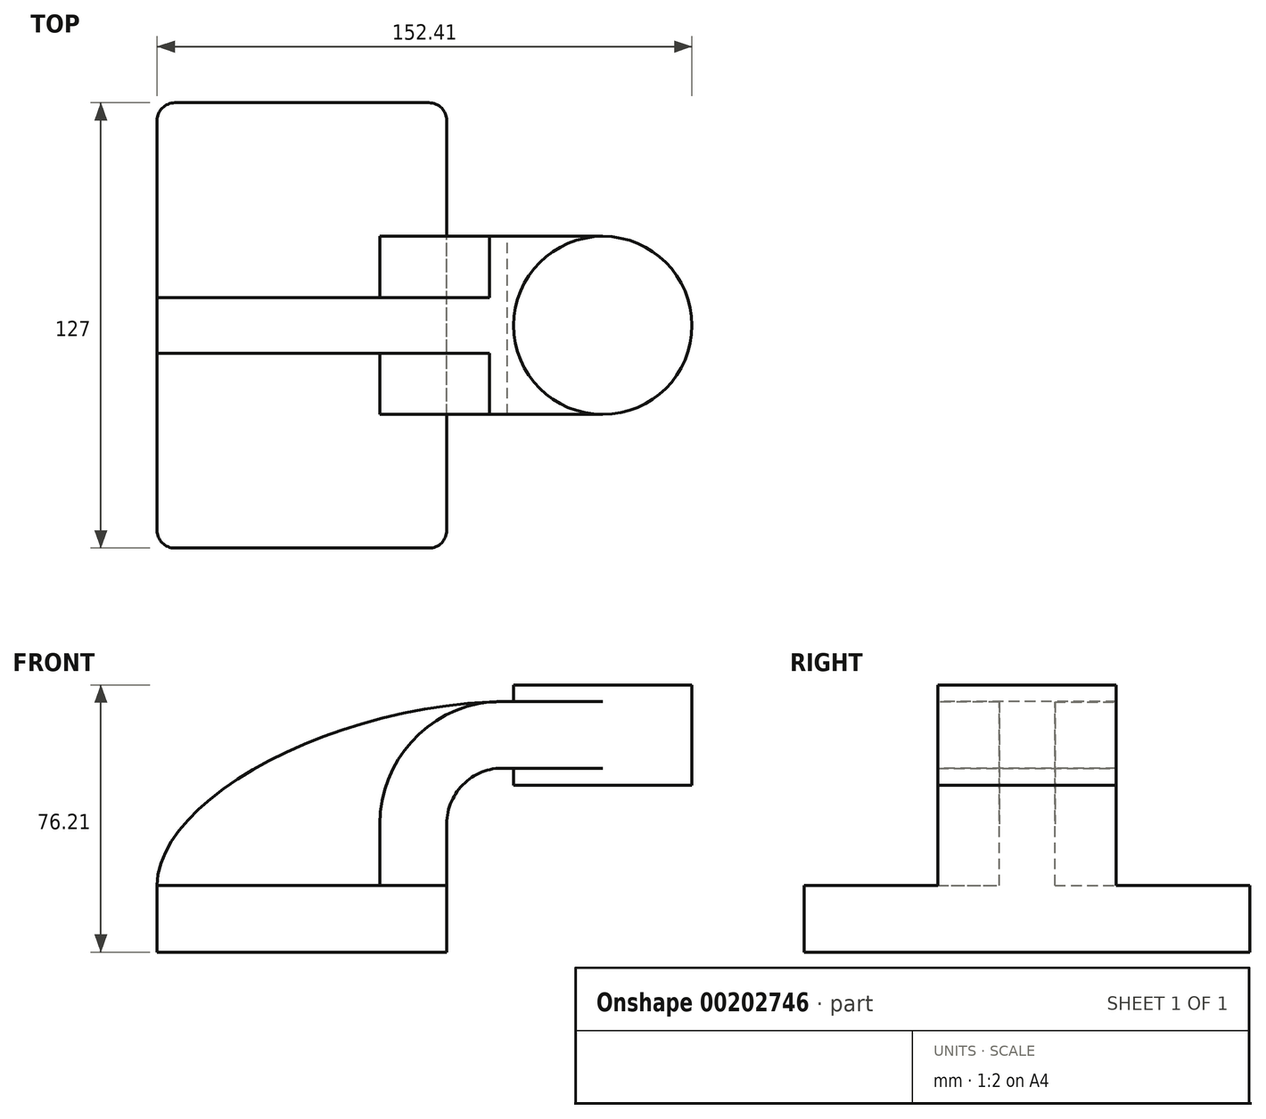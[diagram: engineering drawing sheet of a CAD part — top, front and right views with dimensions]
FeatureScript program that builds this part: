
annotation { "Feature Type Name" : "Feature", "Feature Type Description" : "" }
export const myFeature = defineFeature(function(context is Context, id is Id, definition is map)
    precondition{}
    {
        {
            var Q0;
            Q0=qCreatedBy(makeId("Front.planeOp"),FACE);
            var sketch = newSketch(context, id + "F0", { "sketchPlane" : qUnion([Q0])});
            skLineSegment(sketch, "E0.bottom", {"start": v(-41.28, 9.52) * mm, "end": v(41.28, 9.53) * mm});
            skLineSegment(sketch, "E0.top", {"start": v(-41.28, -9.53) * mm, "end": v(41.28, -9.53) * mm});
            skLineSegment(sketch, "E0.left", {"start": v(-41.28, 9.52) * mm, "end": v(-41.28, -9.53) * mm});
            skLineSegment(sketch, "E0.right", {"start": v(41.28, 9.53) * mm, "end": v(41.28, -9.52) * mm});
            skPoint(sketch, "E0.middle", {"position": v(0, 0) * mm});
            skLineSegment(sketch, "E1.bottom", {"start": v(111.12, 38.1) * mm, "end": v(60.32, 38.1) * mm});
            skLineSegment(sketch, "E1.top", {"start": v(111.12, 66.67) * mm, "end": v(60.32, 66.67) * mm});
            skLineSegment(sketch, "E1.left", {"start": v(111.12, 38.1) * mm, "end": v(111.12, 66.68) * mm});
            skLineSegment(sketch, "E1.right", {"start": v(60.32, 38.1) * mm, "end": v(60.32, 66.67) * mm});
            skPoint(sketch, "E1.middle", {"position": v(85.72, 52.39) * mm});
            skLineSegment(sketch, "E2", {"start": v(41.27, 9.53) * mm, "end": v(41.27, 27.06) * mm});
            skArc(sketch, "E3", {"start": v(41.27, 27.06) * mm, "mid": v(46.4, 38.74) * mm, "end": v(58.47, 42.88) * mm});
            skLineSegment(sketch, "E4", {"start": v(58.47, 42.88) * mm, "end": v(83.46, 42.88) * mm});
            skLineSegment(sketch, "E5.0", {"start": v(59.11, 61.93) * mm, "end": v(83.46, 61.93) * mm});
            skArc(sketch, "E5.1", {"start": v(22.22, 27.06) * mm, "mid": v(33.16, 52.44) * mm, "end": v(59.11, 61.93) * mm});
            skLineSegment(sketch, "E5.2", {"start": v(22.22, 9.53) * mm, "end": v(22.22, 27.06) * mm});
            skFitSpline(sketch, "E6", {"points": [v(-41.28, 9.52) * mm, v(59.11, 61.93) * mm], "startDerivative": vector(0.16, 74.33) * mm, "endDerivative": vector(148.19, 0.72) * mm});
            skLineSegment(sketch, "E7", {"start": v(85.72, 66.67) * mm, "end": v(85.72, 38.1) * mm});
            skLineSegment(sketch, "E8", {"start": v(83.46, 61.93) * mm, "end": v(85.72, 61.93) * mm});
            skLineSegment(sketch, "E9", {"start": v(83.46, 42.88) * mm, "end": v(85.72, 42.88) * mm});
            skSolve(sketch);
        }
        {
            var Q0;
            Q0=makeQuery(id+"F0.imprint","IMPRINT",FACE,{"disambiguationData":[TD([[makeQuery(id+"F0.imprint","IMPRINT",EDGE,{"derivedFrom":sQuery(id+"F0.wireOp",EDGE,"E0.top")}),1.0]])]});
            extrude(context, id + "F1", {"entities" : qUnion([Q0]), "endBound" : BoundingType.SYMMETRIC, "depth" : 127 * mm});
        }
        {
            var Q0;
            {var subQ0=sQuery(id+"F0.wireOp",EDGE,"E8");Q0=makeQuery(id+"F0.imprint","IMPRINT",FACE,{"disambiguationData":[TD([[makeQuery(id+"F0.imprint","IMPRINT",EDGE,{"derivedFrom":subQ0}),-1.0]])]});}
            var Q1;
            {var subQ1=sQuery(id+"F0.wireOp",EDGE,"E2");Q1=makeQuery(id+"F0.imprint","IMPRINT",FACE,{"disambiguationData":[TD([[makeQuery(id+"F0.imprint","IMPRINT",EDGE,{"derivedFrom":subQ1}),1.0]])]});}
            extrude(context, id + "F2", {"entities" : qUnion([Q0, Q1]), "operationType" : NewBodyOperationType.ADD, "endBound" : BoundingType.SYMMETRIC, "depth" : 50.8 * mm});
        }
        {
            var Q0;
            {var subQ3=sQuery(id+"F0.wireOp",EDGE,"E5.2");Q0=makeQuery(id+"F0.imprint","IMPRINT",FACE,{"disambiguationData":[TD([[makeQuery(id+"F0.imprint","IMPRINT",EDGE,{"derivedFrom":subQ3}),1.0]])]});}
            extrude(context, id + "F3", {"entities" : qUnion([Q0]), "operationType" : NewBodyOperationType.ADD, "endBound" : BoundingType.SYMMETRIC, "depth" : 15.88 * mm});
        }
        {
            var Q0;
            {var subQ4=sQuery(id+"F0.wireOp",EDGE,"E1.left");Q0=makeQuery(id+"F0.imprint","IMPRINT",FACE,{"disambiguationData":[TD([[makeQuery(id+"F0.imprint","IMPRINT",EDGE,{"derivedFrom":subQ4}),1.0]])]});}
            var Q1;
            Q1=sQuery(id+"F0.wireOp",EDGE,"E7");
            revolve(context, id + "F4", {"operationType" : NewBodyOperationType.ADD, "entities" : qUnion([Q0]), "axis" : qUnion([Q1]), "revolveType" : RevolveType.FULL});
        }
        {
            var Q0;
            Q0=makeQuery(id+"F1.opExtrude","CAP_EDGE",EDGE,{"disambiguationData":[OSD([sQuery(id+"F0.wireOp",EDGE,"E0.right")])],"isStart":false});
            var Q1;
            Q1=makeQuery(id+"F1.opExtrude","CAP_EDGE",EDGE,{"disambiguationData":[OSD([sQuery(id+"F0.wireOp",EDGE,"E0.left")])],"isStart":false});
            var Q2;
            Q2=makeQuery(id+"F1.opExtrude","CAP_EDGE",EDGE,{"disambiguationData":[OSD([sQuery(id+"F0.wireOp",EDGE,"E0.left")])],"isStart":true});
            var Q3;
            Q3=makeQuery(id+"F1.opExtrude","CAP_EDGE",EDGE,{"disambiguationData":[OSD([sQuery(id+"F0.wireOp",EDGE,"E0.right")])],"isStart":true});
            fillet(context, id + "F5", {"entities" : qUnion([Q0, Q1, Q2, Q3]), "radius" : 5.08 * mm, "tangentPropagation" : true, "allowEdgeOverflow" : false});
        }
    });
